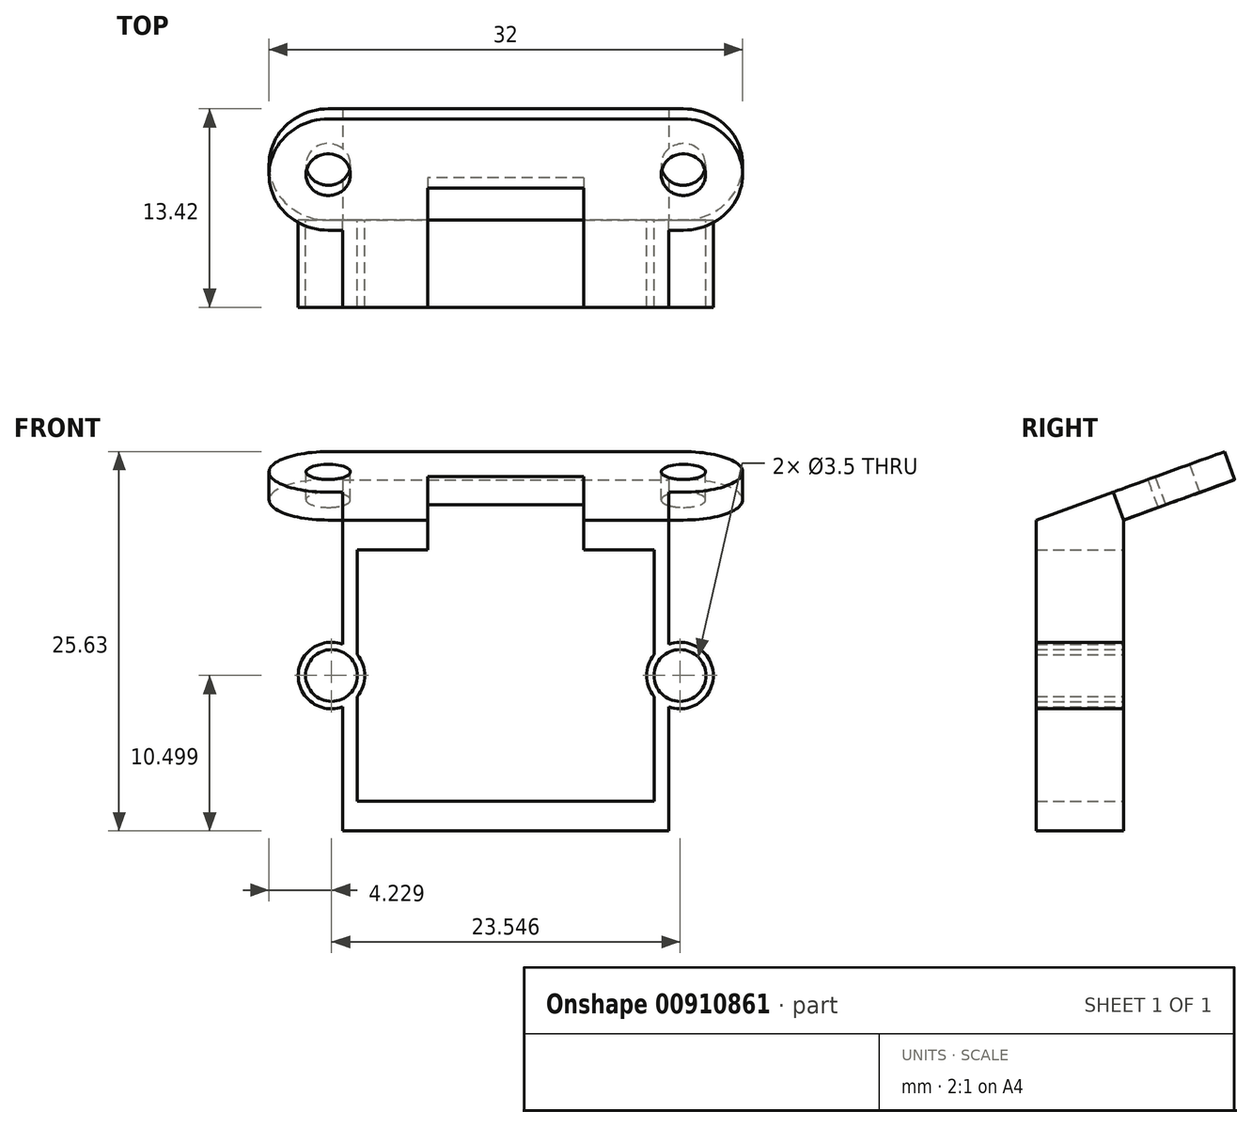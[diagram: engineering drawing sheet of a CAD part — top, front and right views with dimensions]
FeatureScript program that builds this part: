
annotation { "Feature Type Name" : "Feature", "Feature Type Description" : "" }
export const myFeature = defineFeature(function(context is Context, id is Id, definition is map)
    precondition{}
    {
        {
            var Q0;
            Q0=qCreatedBy(makeId("Front.planeOp"),FACE);
            var sketch = newSketch(context, id + "F0", { "sketchPlane" : qUnion([Q0])});
            skCircle(sketch, "E0", {"center": v(-29.91, 23.52) * mm, "radius": 1.75 * mm});
            skCircle(sketch, "E1", {"center": v(-6.37, 23.52) * mm, "radius": 1.75 * mm});
            skCircle(sketch, "E2", {"center": v(-29.91, 23.52) * mm, "radius": 2.25 * mm});
            skCircle(sketch, "E3", {"center": v(-6.37, 23.52) * mm, "radius": 2.25 * mm});
            skLineSegment(sketch, "E4", {"start": v(-8.12, 23.52) * mm, "end": v(-8.12, 32.01) * mm});
            skLineSegment(sketch, "E5", {"start": v(-8.12, 32.01) * mm, "end": v(-28.16, 32.01) * mm});
            skLineSegment(sketch, "E6", {"start": v(-28.16, 32.01) * mm, "end": v(-28.16, 23.52) * mm});
            skLineSegment(sketch, "E7", {"start": v(-29.16, 25.64) * mm, "end": v(-29.16, 34.01) * mm});
            skLineSegment(sketch, "E8", {"start": v(-29.16, 34.01) * mm, "end": v(-7.12, 34.01) * mm});
            skLineSegment(sketch, "E9", {"start": v(-7.12, 34.01) * mm, "end": v(-7.12, 25.64) * mm});
            skLineSegment(sketch, "E10", {"start": v(-28.16, 23.52) * mm, "end": v(-28.16, 15.02) * mm});
            skLineSegment(sketch, "E11", {"start": v(-28.16, 15.02) * mm, "end": v(-8.12, 15.02) * mm});
            skLineSegment(sketch, "E12", {"start": v(-8.12, 15.02) * mm, "end": v(-8.12, 23.52) * mm});
            skLineSegment(sketch, "E13", {"start": v(-7.12, 21.94) * mm, "end": v(-7.12, 13.02) * mm});
            skLineSegment(sketch, "E14", {"start": v(-7.12, 13.02) * mm, "end": v(-29.16, 13.02) * mm});
            skLineSegment(sketch, "E15", {"start": v(-29.16, 13.02) * mm, "end": v(-29.16, 21.94) * mm});
            skSolve(sketch);
        }
        {
            var Q0;
            Q0 = qSketchRegion(id + "F0", true);
            var Q1;
            {var subQ0=sQuery(id+"F0.wireOp",EDGE,"E4");var subQ1=sQuery(id+"F0.wireOp",EDGE,"E3");var subQ2=makeQuery(id+"F0.imprint","INTERSECT",VERTEX,{"derivedFrom":[subQ1,subQ0]});Q1=makeQuery(id+"F0.imprint","IMPRINT",FACE,{"disambiguationData":[TD([[makeQuery(id+"F0.imprint","IMPRINT",EDGE,{"disambiguationData":[TD([[subQ2,-1.0]])],"derivedFrom":subQ1}),1.0]])]});}
            var Q2;
            {var subQ0=sQuery(id+"F0.wireOp",EDGE,"E6");var subQ1=sQuery(id+"F0.wireOp",EDGE,"E2");var subQ2=makeQuery(id+"F0.imprint","INTERSECT",VERTEX,{"derivedFrom":[subQ1,subQ0]});Q2=makeQuery(id+"F0.imprint","IMPRINT",FACE,{"disambiguationData":[TD([[makeQuery(id+"F0.imprint","IMPRINT",EDGE,{"disambiguationData":[TD([[subQ2,1.0]])],"derivedFrom":subQ1}),1.0]])]});}
            extrude(context, id + "F1", {"entities" : qUnion([Q0, Q1, Q2]), "depth" : 5.9 * mm, "offsetDistance" : 25.4 * mm});
        }
        {
            var Q0;
            Q0=makeQuery(id+"F1.opExtrude","SWEPT_FACE",FACE,{"disambiguationData":[OSD([sQuery(id+"F0.wireOp",EDGE,"E9")])]});
            var sketch = newSketch(context, id + "F2", { "sketchPlane" : qUnion([Q0])});
            skLineSegment(sketch, "E16", {"start": v(-5.9, 34.01) * mm, "end": v(6.83, 38.65) * mm});
            skLineSegment(sketch, "E17", {"start": v(6.83, 38.65) * mm, "end": v(7.52, 36.75) * mm});
            skLineSegment(sketch, "E18", {"start": v(7.52, 36.75) * mm, "end": v(0, 34.01) * mm});
            skSolve(sketch);
        }
        {
            var Q0;
            Q0=makeQuery(id+"F2.imprint","IMPRINT",FACE,{"disambiguationData":[TD([[makeQuery(id+"F2.imprint","IMPRINT",EDGE,{"derivedFrom":sQuery(id+"F2.wireOp",EDGE,"E16")}),-1.0]])]});
            extrude(context, id + "F3", {"entities" : qUnion([Q0]), "operationType" : NewBodyOperationType.ADD, "oppositeDirection" : true, "depth" : 20.04 * mm + 2 * mm, "offsetDistance" : 25.4 * mm});
        }
        {
            var Q0;
            Q0=makeQuery(id+"F3.opExtrude","SWEPT_FACE",FACE,{"disambiguationData":[OSD([sQuery(id+"F2.wireOp",EDGE,"E16")])]});
            var sketch = newSketch(context, id + "F4", { "sketchPlane" : qUnion([Q0])});
            skLineSegment(sketch, "E19", {"start": v(-18.14, 19.63) * mm, "end": v(-30.14, 19.63) * mm});
            skLineSegment(sketch, "E20", {"start": v(-18.14, 19.63) * mm, "end": v(-6.14, 19.63) * mm});
            skLineSegment(sketch, "E21", {"start": v(-35.14, 11.63) * mm, "end": v(-29.16, 11.63) * mm});
            skLineSegment(sketch, "E22", {"start": v(-29.16, 11.63) * mm, "end": v(-1.14, 11.63) * mm});
            skLineSegment(sketch, "E23", {"start": v(-30.14, 19.63) * mm, "end": v(-30.14, 11.63) * mm});
            skLineSegment(sketch, "E24", {"start": v(-35.14, 11.63) * mm, "end": v(-30.14, 11.63) * mm});
            skLineSegment(sketch, "E25", {"start": v(-6.14, 19.63) * mm, "end": v(-6.14, 11.63) * mm});
            skLineSegment(sketch, "E26", {"start": v(-1.14, 11.63) * mm, "end": v(-6.14, 11.63) * mm});
            skCircle(sketch, "E27", {"center": v(-30.14, 15.63) * mm, "radius": 1.5 * mm});
            skCircle(sketch, "E28", {"center": v(-6.14, 15.63) * mm, "radius": 1.5 * mm});
            skLineSegment(sketch, "E29.bottom", {"start": v(-30.14, 15.63) * mm, "end": v(-30.14, 15.63) * mm});
            skLineSegment(sketch, "E29.top", {"start": v(-30.14, 11.63) * mm, "end": v(-30.14, 11.63) * mm});
            skLineSegment(sketch, "E29.left", {"start": v(-30.14, 15.63) * mm, "end": v(-30.14, 11.63) * mm});
            skLineSegment(sketch, "E29.right", {"start": v(-30.14, 15.63) * mm, "end": v(-30.14, 11.63) * mm});
            skArc(sketch, "E30", {"start": v(-30.14, 19.63) * mm, "mid": v(-34.14, 15.63) * mm, "end": v(-30.14, 11.63) * mm});
            skArc(sketch, "E31", {"start": v(-6.14, 11.63) * mm, "mid": v(-2.14, 15.63) * mm, "end": v(-6.14, 19.63) * mm});
            skSolve(sketch);
        }
        {
            var Q0;
            Q0 = qSketchRegion(id + "F4", true);
            extrude(context, id + "F5", {"entities" : qUnion([Q0]), "operationType" : NewBodyOperationType.ADD, "oppositeDirection" : true, "depth" : 2 * mm, "offsetDistance" : 25.4 * mm});
        }
        {
            var Q0;
            Q0=makeQuery(id+"F5.boolean.opBoolean","MERGE",FACE,{"derivedFrom":[makeQuery(id+"F3.opExtrude","SWEPT_FACE",FACE,{"disambiguationData":[OSD([sQuery(id+"F2.wireOp",EDGE,"E16")])]}),makeQuery(id+"F5.opExtrude","CAP_FACE",FACE,{"disambiguationData":[OSD([sQuery(id+"F4.wireOp",EDGE,"E19"),sQuery(id+"F4.wireOp",EDGE,"E20"),sQuery(id+"F4.wireOp",EDGE,"E21"),sQuery(id+"F4.wireOp",EDGE,"E22"),sQuery(id+"F4.wireOp",EDGE,"E27"),sQuery(id+"F4.wireOp",EDGE,"E28"),sQuery(id+"F4.wireOp",EDGE,"E30"),sQuery(id+"F4.wireOp",EDGE,"E31")])],"isStart":true})]});
            var sketch = newSketch(context, id + "F6", { "sketchPlane" : qUnion([Q0])});
            skCircle(sketch, "E32", {"center": v(-30.14, 15.63) * mm, "radius": 1.5 * mm});
            skCircle(sketch, "E33", {"center": v(-6.14, 15.63) * mm, "radius": 1.5 * mm});
            skSolve(sketch);
        }
        {
            var Q0;
            Q0 = qSketchRegion(id + "F6", true);
            extrude(context, id + "F7", {"entities" : qUnion([Q0]), "operationType" : NewBodyOperationType.REMOVE, "oppositeDirection" : true, "depth" : 25.4 * mm, "offsetDistance" : 25.4 * mm});
        }
        {
            var Q0;
            Q0=makeQuery(id+"F5.boolean.opBoolean","MERGE",FACE,{"derivedFrom":[makeQuery(id+"F3.opExtrude","SWEPT_FACE",FACE,{"disambiguationData":[OSD([sQuery(id+"F2.wireOp",EDGE,"E16")])]}),makeQuery(id+"F5.opExtrude","CAP_FACE",FACE,{"disambiguationData":[OSD([sQuery(id+"F4.wireOp",EDGE,"E19"),sQuery(id+"F4.wireOp",EDGE,"E20"),sQuery(id+"F4.wireOp",EDGE,"E21"),sQuery(id+"F4.wireOp",EDGE,"E22"),sQuery(id+"F4.wireOp",EDGE,"E27"),sQuery(id+"F4.wireOp",EDGE,"E28"),sQuery(id+"F4.wireOp",EDGE,"E30"),sQuery(id+"F4.wireOp",EDGE,"E31")])],"isStart":true})]});
            var sketch = newSketch(context, id + "F8", { "sketchPlane" : qUnion([Q0])});
            skLineSegment(sketch, "E34.bottom", {"start": v(-12.87, 14.68) * mm, "end": v(-23.4, 14.68) * mm});
            skLineSegment(sketch, "E34.top", {"start": v(-12.87, -2.5) * mm, "end": v(-23.4, -2.5) * mm});
            skLineSegment(sketch, "E34.left", {"start": v(-12.87, 14.68) * mm, "end": v(-12.87, -2.5) * mm});
            skLineSegment(sketch, "E34.right", {"start": v(-23.4, 14.68) * mm, "end": v(-23.4, -2.5) * mm});
            skPoint(sketch, "E34.middle", {"position": v(-18.14, 6.09) * mm});
            skSolve(sketch);
        }
        {
            var Q0;
            Q0 = qSketchRegion(id + "F8", true);
            extrude(context, id + "F9", {"entities" : qUnion([Q0]), "operationType" : NewBodyOperationType.REMOVE, "oppositeDirection" : true, "depth" : 5.36 * mm, "offsetDistance" : 25.4 * mm});
        }
    });
